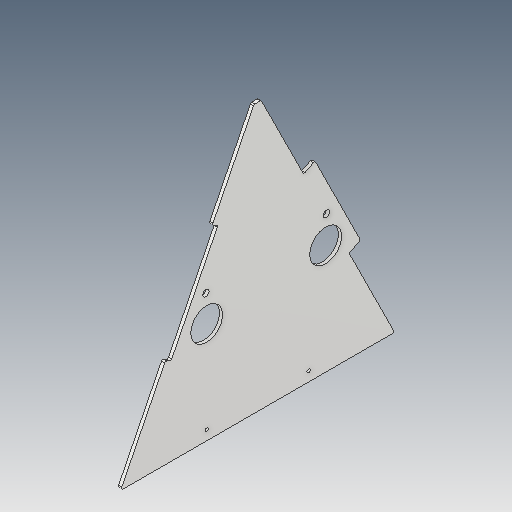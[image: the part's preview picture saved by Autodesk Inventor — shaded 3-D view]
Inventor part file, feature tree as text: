
AUTODESK INVENTOR PART (.ipt)
format: ipt  version: 2023.5 (Build 275446000, 446)  size: 110,080 bytes
history: native  units: in
note: dims shown in document units (in); Inventor stores cm internally (conversion verified against a paired STEP export)
features: fillet x1
ambient origin geometry x8: Origin, YZ Plane, XZ Plane, XY Plane, X Axis, Y Axis, Z Axis, Center Point
bodies: Solid1 (feature_tree)
feature tree (1):
  fillet  "Fillet1"  [1 undecoded]
note: 1 required parameter value undecoded (feature->parameter linkage not recoverable at this tier; creation-order binding heuristic only, values carry confidence <= 0.55)
